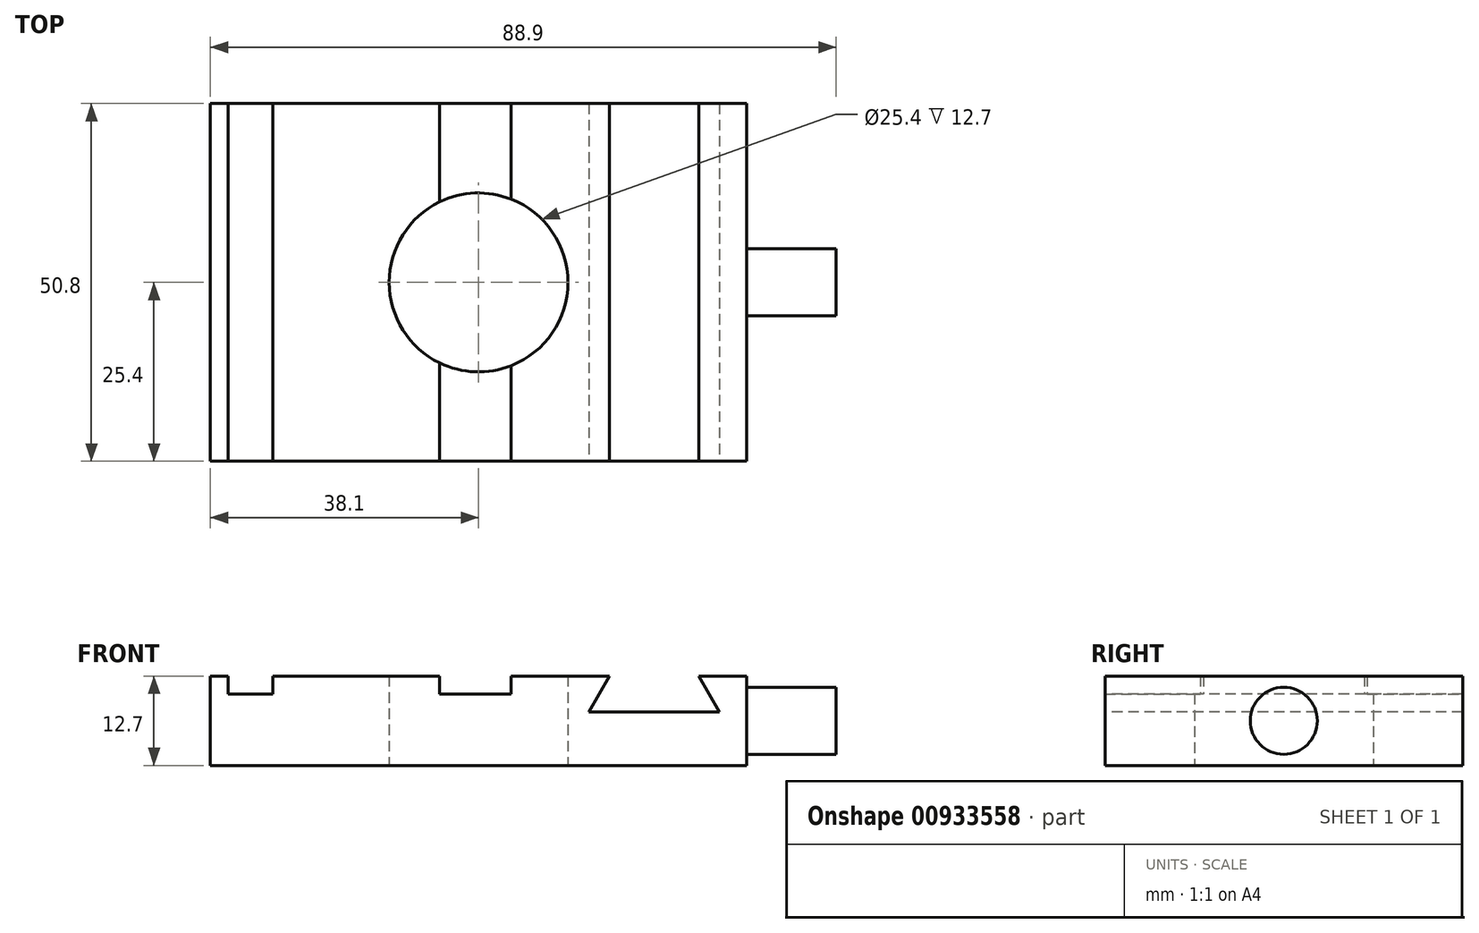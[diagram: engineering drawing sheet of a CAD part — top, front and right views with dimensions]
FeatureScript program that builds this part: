
annotation { "Feature Type Name" : "Feature", "Feature Type Description" : "" }
export const myFeature = defineFeature(function(context is Context, id is Id, definition is map)
    precondition{}
    {
        {
            var Q0;
            Q0=qCreatedBy(makeId("Top.planeOp"),FACE);
            var sketch = newSketch(context, id + "F0", { "sketchPlane" : qUnion([Q0])});
            skLineSegment(sketch, "E0.bottom", {"start": v(-38.1, 25.4) * mm, "end": v(38.1, 25.4) * mm});
            skLineSegment(sketch, "E0.top", {"start": v(-38.1, -25.4) * mm, "end": v(38.1, -25.4) * mm});
            skLineSegment(sketch, "E0.left", {"start": v(-38.1, 25.4) * mm, "end": v(-38.1, -25.4) * mm});
            skLineSegment(sketch, "E0.right", {"start": v(38.1, 25.4) * mm, "end": v(38.1, -25.4) * mm});
            skPoint(sketch, "E0.middle", {"position": v(0, 0) * mm});
            skCircle(sketch, "E1", {"center": v(0, 0) * mm, "radius": 12.7 * mm});
            skSolve(sketch);
        }
        {
            var Q0;
            Q0=makeQuery(id+"F0.imprint","IMPRINT",FACE,{"disambiguationData":[TD([[makeQuery(id+"F0.imprint","IMPRINT",EDGE,{"derivedFrom":sQuery(id+"F0.wireOp",EDGE,"E0.bottom")}),-1.0]])]});
            extrude(context, id + "F1", {"entities" : qUnion([Q0]), "depth" : 12.7 * mm, "offsetDistance" : 25.4 * mm});
        }
        {
            var Q0;
            Q0=makeQuery(id+"F1.opExtrude","CAP_FACE",FACE,{"disambiguationData":[OSD([sQuery(id+"F0.wireOp",EDGE,"E0.bottom"),sQuery(id+"F0.wireOp",EDGE,"E0.top"),sQuery(id+"F0.wireOp",EDGE,"E0.left"),sQuery(id+"F0.wireOp",EDGE,"E0.right"),sQuery(id+"F0.wireOp",EDGE,"E1")])],"isStart":false});
            var sketch = newSketch(context, id + "F2", { "sketchPlane" : qUnion([Q0])});
            skLineSegment(sketch, "E2.bottom", {"start": v(-35.56, 25.4) * mm, "end": v(-29.21, 25.4) * mm});
            skLineSegment(sketch, "E2.top", {"start": v(-35.56, -25.4) * mm, "end": v(-29.21, -25.4) * mm});
            skLineSegment(sketch, "E2.left", {"start": v(-35.56, 25.4) * mm, "end": v(-35.56, -25.4) * mm});
            skLineSegment(sketch, "E2.right", {"start": v(-29.21, 25.4) * mm, "end": v(-29.21, -25.4) * mm});
            skPoint(sketch, "E3", {"position": v(0, 0) * mm});
            skPoint(sketch, "E4", {"position": v(0, 25.4) * mm});
            skLineSegment(sketch, "E5", {"start": v(-5.54, 25.4) * mm, "end": v(-5.54, -25.4) * mm});
            skLineSegment(sketch, "E6", {"start": v(-5.54, -25.4) * mm, "end": v(4.62, -25.4) * mm});
            skLineSegment(sketch, "E7", {"start": v(4.62, -25.4) * mm, "end": v(4.62, 25.4) * mm});
            skLineSegment(sketch, "E8", {"start": v(4.62, 25.4) * mm, "end": v(-5.54, 25.4) * mm});
            skLineSegment(sketch, "E9", {"start": v(0, 25.4) * mm, "end": v(0, -25.4) * mm, "construction": true});
            skSolve(sketch);
        }
        {
            var Q0;
            {var subQ0=sQuery(id+"F2.wireOp",EDGE,"E5");var subQ1=makeQuery(id+"F1.opExtrude","CAP_EDGE",EDGE,{"disambiguationData":[OSD([sQuery(id+"F0.wireOp",EDGE,"E1")])],"isStart":false});var subQ2=makeQuery(id+"F2.imprint","INTERSECT",VERTEX,{"disambiguationData":[OD(0.0)],"derivedFrom":[subQ1,subQ0]});Q0=makeQuery(id+"F2.imprint","IMPRINT",FACE,{"disambiguationData":[TD([[makeQuery(id+"F2.imprint","IMPRINT",EDGE,{"disambiguationData":[TD([[subQ2,-1.0]])],"derivedFrom":subQ0}),1.0]])]});}
            var Q1;
            Q1=makeQuery(id+"F2.imprint","IMPRINT",FACE,{"disambiguationData":[TD([[makeQuery(id+"F2.imprint","IMPRINT",EDGE,{"derivedFrom":sQuery(id+"F2.wireOp",EDGE,"E2.bottom")}),-1.0]])]});
            var Q2;
            {var subQ0=sQuery(id+"F2.wireOp",EDGE,"E6");Q2=makeQuery(id+"F2.imprint","IMPRINT",FACE,{"disambiguationData":[TD([[makeQuery(id+"F2.imprint","IMPRINT",EDGE,{"derivedFrom":subQ0}),1.0]])]});}
            var Q3;
            {var subQ0=sQuery(id+"F2.wireOp",EDGE,"E8");Q3=makeQuery(id+"F2.imprint","IMPRINT",FACE,{"disambiguationData":[TD([[makeQuery(id+"F2.imprint","IMPRINT",EDGE,{"derivedFrom":subQ0}),-1.0]])]});}
            extrude(context, id + "F3", {"entities" : qUnion([Q0, Q1, Q2, Q3]), "operationType" : NewBodyOperationType.REMOVE, "oppositeDirection" : true, "depth" : 2.54 * mm, "offsetDistance" : 25.4 * mm});
        }
        {
            var Q0;
            Q0=makeQuery(id+"F1.opExtrude","SWEPT_FACE",FACE,{"disambiguationData":[OSD([sQuery(id+"F0.wireOp",EDGE,"E0.top")])]});
            var sketch = newSketch(context, id + "F4", { "sketchPlane" : qUnion([Q0])});
            skLineSegment(sketch, "E10", {"start": v(18.6, 12.7) * mm, "end": v(15.66, 7.62) * mm});
            skLineSegment(sketch, "E11", {"start": v(15.66, 7.62) * mm, "end": v(34.23, 7.62) * mm});
            skLineSegment(sketch, "E12", {"start": v(34.23, 7.62) * mm, "end": v(31.3, 12.7) * mm});
            skLineSegment(sketch, "E13", {"start": v(31.3, 12.7) * mm, "end": v(18.6, 12.7) * mm});
            skLineSegment(sketch, "E14", {"start": v(24.94, 7.62) * mm, "end": v(24.94, 12.7) * mm, "construction": true});
            skSolve(sketch);
        }
        {
            var Q0;
            Q0=makeQuery(id+"F4.imprint","IMPRINT",FACE,{"disambiguationData":[TD([[makeQuery(id+"F4.imprint","IMPRINT",EDGE,{"derivedFrom":sQuery(id+"F4.wireOp",EDGE,"E10")}),1.0]])]});
            extrude(context, id + "F5", {"entities" : qUnion([Q0]), "operationType" : NewBodyOperationType.REMOVE, "endBound" : BoundingType.THROUGH_ALL, "oppositeDirection" : true, "depth" : 25.4 * mm, "offsetDistance" : 25.4 * mm});
        }
        {
            var Q0;
            Q0=makeQuery(id+"F1.opExtrude","SWEPT_FACE",FACE,{"disambiguationData":[OSD([sQuery(id+"F0.wireOp",EDGE,"E0.right")])]});
            var sketch = newSketch(context, id + "F6", { "sketchPlane" : qUnion([Q0])});
            skCircle(sketch, "E15", {"center": v(0, 6.35) * mm, "radius": 4.76 * mm});
            skPoint(sketch, "E15.centerSnap0", {"position": v(-25.4, 6.35) * mm});
            skPoint(sketch, "E15.centerSnap1", {"position": v(0, 12.7) * mm});
            skSolve(sketch);
        }
        {
            var Q0;
            Q0=makeQuery(id+"F6.imprint","IMPRINT",FACE,{"disambiguationData":[TD([[makeQuery(id+"F6.imprint","IMPRINT",EDGE,{"derivedFrom":sQuery(id+"F6.wireOp",EDGE,"E15")}),1.0]])]});
            extrude(context, id + "F7", {"entities" : qUnion([Q0]), "operationType" : NewBodyOperationType.ADD, "depth" : 12.7 * mm, "offsetDistance" : 25.4 * mm});
        }
    });
